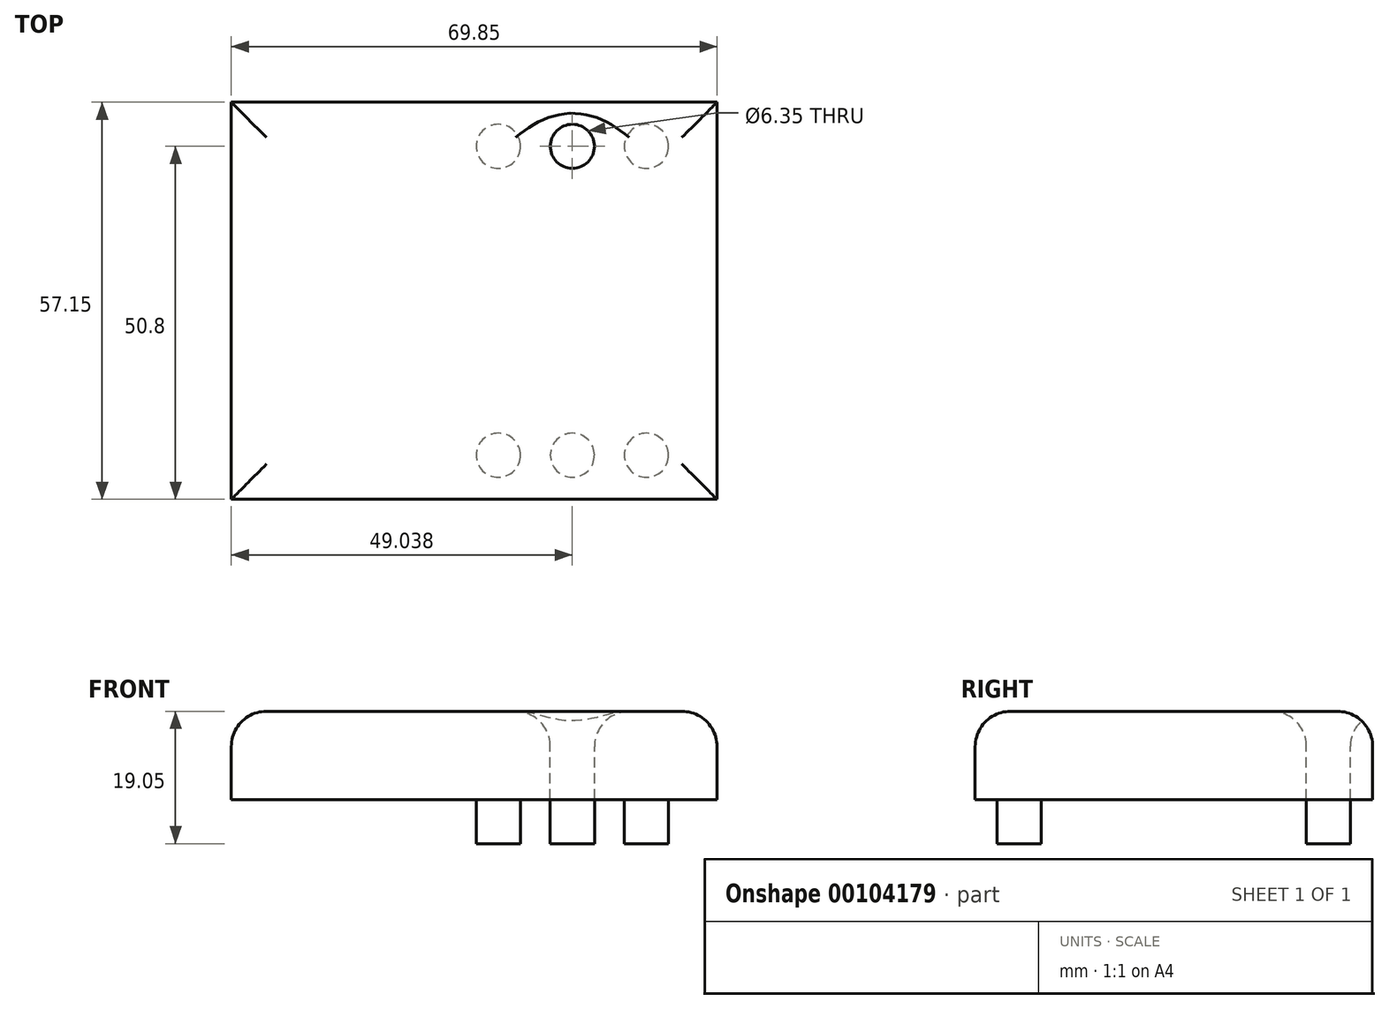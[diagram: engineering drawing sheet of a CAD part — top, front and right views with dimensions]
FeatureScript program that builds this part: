
annotation { "Feature Type Name" : "Feature", "Feature Type Description" : "" }
export const myFeature = defineFeature(function(context is Context, id is Id, definition is map)
    precondition{}
    {
        {
            var Q0;
            Q0=qCreatedBy(makeId("Top.planeOp"),FACE);
            var sketch = newSketch(context, id + "F0", { "sketchPlane" : qUnion([Q0])});
            skLineSegment(sketch, "E0.bottom", {"start": v(-38.4, 50.8) * mm, "end": v(31.46, 50.8) * mm});
            skLineSegment(sketch, "E0.top", {"start": v(-38.4, -6.35) * mm, "end": v(31.46, -6.35) * mm});
            skLineSegment(sketch, "E0.left", {"start": v(-38.4, 50.8) * mm, "end": v(-38.4, -6.35) * mm});
            skLineSegment(sketch, "E0.right", {"start": v(31.46, 50.8) * mm, "end": v(31.46, -6.35) * mm});
            skLineSegment(sketch, "E1", {"start": v(21.3, 44.45) * mm, "end": v(0, 44.45) * mm});
            skLineSegment(sketch, "E2", {"start": v(0, 0) * mm, "end": v(21.3, 0) * mm});
            skCircle(sketch, "E3", {"center": v(0, 0) * mm, "radius": 3.18 * mm});
            skCircle(sketch, "E4", {"center": v(10.65, 0) * mm, "radius": 3.18 * mm});
            skCircle(sketch, "E5", {"center": v(21.3, 0) * mm, "radius": 3.18 * mm});
            skCircle(sketch, "E6", {"center": v(21.3, 44.45) * mm, "radius": 3.18 * mm});
            skCircle(sketch, "E7", {"center": v(10.65, 44.45) * mm, "radius": 3.18 * mm});
            skCircle(sketch, "E8", {"center": v(0, 44.45) * mm, "radius": 3.18 * mm});
            skLineSegment(sketch, "E9", {"start": v(21.3, 44.45) * mm, "end": v(21.3, 50.8) * mm});
            skLineSegment(sketch, "E10", {"start": v(21.3, 44.45) * mm, "end": v(31.46, 44.45) * mm});
            skLineSegment(sketch, "E11", {"start": v(21.3, 0) * mm, "end": v(21.3, -6.35) * mm});
            skLineSegment(sketch, "E12", {"start": v(21.3, 0) * mm, "end": v(31.46, 0) * mm});
            skSolve(sketch);
        }
        {
            var Q0;
            Q0 = qSketchRegion(id + "F0", true);
            extrude(context, id + "F1", {"entities" : qUnion([Q0]), "oppositeDirection" : true, "depth" : 12.7 * mm});
        }
        {
            var Q0;
            Q0=makeQuery(id+"F0.imprint","IMPRINT",FACE,{"disambiguationData":[TD([[makeQuery(id+"F0.imprint","IMPRINT",EDGE,{"derivedFrom":sQuery(id+"F0.wireOp",EDGE,"E3")}),1.0]])]});
            var Q1;
            {var subQ0=sQuery(id+"F0.wireOp",EDGE,"E4");var subQ1=sQuery(id+"F0.wireOp",EDGE,"E2");var subQ2=makeQuery(id+"F0.imprint","INTERSECT",VERTEX,{"disambiguationData":[OD(0.0)],"derivedFrom":[subQ1,subQ0]});Q1=makeQuery(id+"F0.imprint","IMPRINT",FACE,{"disambiguationData":[TD([[makeQuery(id+"F0.imprint","IMPRINT",EDGE,{"disambiguationData":[TD([[subQ2,-1.0]])],"derivedFrom":subQ1}),-1.0]])]});}
            var Q2;
            {var subQ0=sQuery(id+"F0.wireOp",EDGE,"E4");var subQ1=sQuery(id+"F0.wireOp",EDGE,"E2");var subQ2=makeQuery(id+"F0.imprint","INTERSECT",VERTEX,{"disambiguationData":[OD(0.0)],"derivedFrom":[subQ1,subQ0]});Q2=makeQuery(id+"F0.imprint","IMPRINT",FACE,{"disambiguationData":[TD([[makeQuery(id+"F0.imprint","IMPRINT",EDGE,{"disambiguationData":[TD([[subQ2,-1.0]])],"derivedFrom":subQ1}),1.0]])]});}
            var Q3;
            Q3=makeQuery(id+"F0.imprint","IMPRINT",FACE,{"disambiguationData":[TD([[makeQuery(id+"F0.imprint","IMPRINT",EDGE,{"derivedFrom":sQuery(id+"F0.wireOp",EDGE,"E5")}),1.0]])]});
            var Q4;
            Q4=makeQuery(id+"F0.imprint","IMPRINT",FACE,{"disambiguationData":[TD([[makeQuery(id+"F0.imprint","IMPRINT",EDGE,{"derivedFrom":sQuery(id+"F0.wireOp",EDGE,"E8")}),1.0]])]});
            var Q5;
            {var subQ0=sQuery(id+"F0.wireOp",EDGE,"E7");var subQ1=sQuery(id+"F0.wireOp",EDGE,"E1");var subQ2=makeQuery(id+"F0.imprint","INTERSECT",VERTEX,{"disambiguationData":[OD(0.0)],"derivedFrom":[subQ1,subQ0]});Q5=makeQuery(id+"F0.imprint","IMPRINT",FACE,{"disambiguationData":[TD([[makeQuery(id+"F0.imprint","IMPRINT",EDGE,{"disambiguationData":[TD([[subQ2,1.0]])],"derivedFrom":subQ1}),1.0]])]});}
            var Q6;
            {var subQ0=sQuery(id+"F0.wireOp",EDGE,"E7");var subQ1=sQuery(id+"F0.wireOp",EDGE,"E1");var subQ2=makeQuery(id+"F0.imprint","INTERSECT",VERTEX,{"disambiguationData":[OD(0.0)],"derivedFrom":[subQ1,subQ0]});Q6=makeQuery(id+"F0.imprint","IMPRINT",FACE,{"disambiguationData":[TD([[makeQuery(id+"F0.imprint","IMPRINT",EDGE,{"disambiguationData":[TD([[subQ2,1.0]])],"derivedFrom":subQ1}),-1.0]])]});}
            var Q7;
            Q7=makeQuery(id+"F0.imprint","IMPRINT",FACE,{"disambiguationData":[TD([[makeQuery(id+"F0.imprint","IMPRINT",EDGE,{"derivedFrom":sQuery(id+"F0.wireOp",EDGE,"E6")}),1.0]])]});
            extrude(context, id + "F2", {"entities" : qUnion([Q0, Q1, Q2, Q3, Q4, Q5, Q6, Q7]), "operationType" : NewBodyOperationType.ADD, "oppositeDirection" : true, "depth" : 19.05 * mm});
        }
        {
            var Q0;
            {var subQ0=sQuery(id+"F0.wireOp",EDGE,"E8");var subQ1=sQuery(id+"F0.wireOp",EDGE,"E7");var subQ2=sQuery(id+"F0.wireOp",EDGE,"E6");var subQ3=sQuery(id+"F0.wireOp",EDGE,"E5");var subQ4=sQuery(id+"F0.wireOp",EDGE,"E4");var subQ5=sQuery(id+"F0.wireOp",EDGE,"E3");Q0=makeQuery(id+"F2.boolean.opBoolean","MERGE",FACE,{"derivedFrom":[makeQuery(id+"F1.opExtrude","CAP_FACE",FACE,{"disambiguationData":[OSD([sQuery(id+"F0.wireOp",EDGE,"E0.bottom"),sQuery(id+"F0.wireOp",EDGE,"E0.top"),sQuery(id+"F0.wireOp",EDGE,"E0.left"),sQuery(id+"F0.wireOp",EDGE,"E0.right"),subQ5,subQ4,subQ3,subQ2,subQ1,subQ0])],"isStart":true}),makeQuery(id+"F2.opExtrude","CAP_FACE",FACE,{"disambiguationData":[OSD([subQ5])],"isStart":true}),makeQuery(id+"F2.opExtrude","CAP_FACE",FACE,{"disambiguationData":[OSD([subQ4])],"isStart":true}),makeQuery(id+"F2.opExtrude","CAP_FACE",FACE,{"disambiguationData":[OSD([subQ3])],"isStart":true}),makeQuery(id+"F2.opExtrude","CAP_FACE",FACE,{"disambiguationData":[OSD([subQ2])],"isStart":true}),makeQuery(id+"F2.opExtrude","CAP_FACE",FACE,{"disambiguationData":[OSD([subQ1])],"isStart":true}),makeQuery(id+"F2.opExtrude","CAP_FACE",FACE,{"disambiguationData":[OSD([subQ0])],"isStart":true})]});}
            fillet(context, id + "F3", {"entities" : qUnion([Q0]), "radius" : 5.08 * mm, "tangentPropagation" : true, "allowEdgeOverflow" : false});
        }
    });
